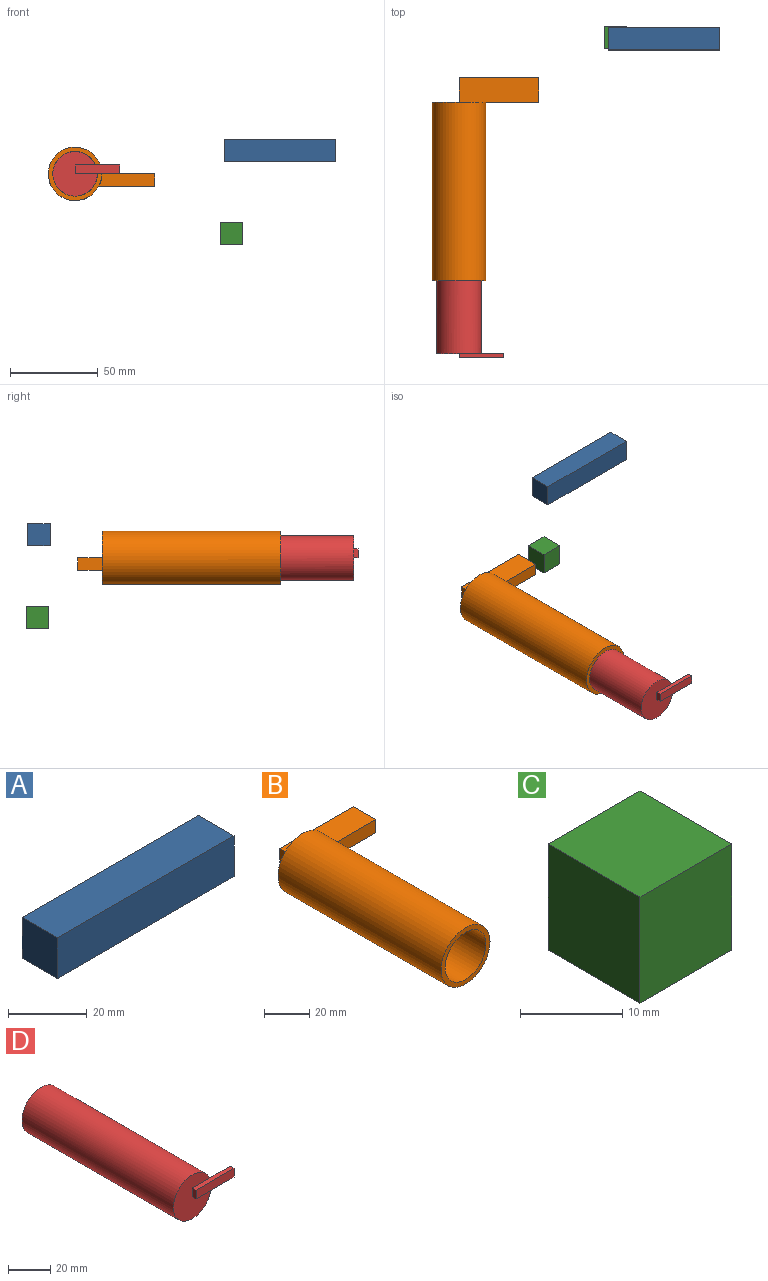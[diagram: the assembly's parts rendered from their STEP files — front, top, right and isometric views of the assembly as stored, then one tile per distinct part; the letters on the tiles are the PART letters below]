
ASSEMBLY  parts=4 mates=1
PART A: 6 faces, bbox 63.5x12.7x12.7 mm
  f0: plane 63.5x12.7mm, normal (0,0,-1), area 806.5mm2, adj f1,f3,f4,f5
  f1: plane 12.7x12.7mm, normal (1,0,0), area 161.3mm2, adj f0,f2,f4,f5
  f2: plane 63.5x12.7mm, normal (0,0,1), area 806.5mm2, adj f1,f3,f4,f5
  f3: plane 12.7x12.7mm, normal (-1,0,0), area 161.3mm2, adj f0,f2,f4,f5
  f4: plane 63.5x12.7mm, normal (0,-1,0), area 806.5mm2, adj f0,f1,f2,f3
  f5: plane 63.5x12.7mm, normal (0,1,0), area 806.5mm2, adj f0,f1,f2,f3
PART B: 11 faces, bbox 60.8x115.6x30.5 mm
  f0: cylinder r=15.24mm len=101.6mm, axis (0,1,0), area 9728.8mm2, adj f1,f2,f9
  f1: plane 30.48x30.48mm, normal (0,-1,0), area 223mm2, adj f0,f3
  f2: plane 30.48x30.48mm, normal (0,1,0), area 624.7mm2, adj f0,f5,f6,f7
  f3: cylinder r=12.7mm len=99.06mm, axis (0,1,0), area 7904.6mm2, adj f1,f4
  f4: plane 25.4x25.4mm, normal (0,-1,0), area 506.7mm2, adj f3
  f5: plane 45.53x14mm, normal (0,0,-1), area 637.3mm2, adj f2,f6,f8,f9,f10
  f6: plane 14x7.16mm, normal (-1,0,0), area 100.2mm2, adj f2,f5,f7,f10
  f7: plane 45.53x14mm, normal (0,0,1), area 637.3mm2, adj f2,f6,f8,f9,f10
  f8: plane 14x7.16mm, normal (1,0,0), area 100.2mm2, adj f5,f7,f9,f10
  f9: plane 32.08x7.16mm, normal (0,-1,0), area 221.1mm2, adj f0,f5,f7,f8
  f10: plane 45.53x7.16mm, normal (0,1,0), area 326.1mm2, adj f5,f6,f7,f8
PART C: 6 faces, bbox 12.7x12.7x12.7 mm
  f0: plane 12.7x12.7mm, normal (0,0,-1), area 161.3mm2, adj f1,f3,f4,f5
  f1: plane 12.7x12.7mm, normal (1,0,0), area 161.3mm2, adj f0,f2,f4,f5
  f2: plane 12.7x12.7mm, normal (0,0,1), area 161.3mm2, adj f1,f3,f4,f5
  f3: plane 12.7x12.7mm, normal (-1,0,0), area 161.3mm2, adj f0,f2,f4,f5
  f4: plane 12.7x12.7mm, normal (0,-1,0), area 161.3mm2, adj f0,f1,f2,f3
  f5: plane 12.7x12.7mm, normal (0,1,0), area 161.3mm2, adj f0,f1,f2,f3
PART D: 9 faces, bbox 38.1x104.1x25.4 mm
  f0: plane 25.4x25.4mm, normal (0,-1,0), area 444mm2, adj f1,f4,f5,f6
  f1: cylinder r=12.7mm len=101.6mm, axis (0,1,0), area 8107.3mm2, adj f0,f2,f3
  f2: plane 25.4x25.4mm, normal (0,1,0), area 506.7mm2, adj f1
  f3: plane 13.76x5.08mm, normal (0,1,0), area 66.3mm2, adj f1,f4,f6,f7
  f4: plane 25.4x2.54mm, normal (0,0,1), area 64.5mm2, adj f0,f3,f5,f7,f8
  f5: plane 5.08x2.54mm, normal (-1,0,0), area 12.9mm2, adj f0,f4,f6,f8
  f6: plane 25.4x2.54mm, normal (0,0,-1), area 64.5mm2, adj f0,f3,f5,f7,f8
  f7: plane 5.08x2.54mm, normal (1,0,0), area 12.9mm2, adj f3,f4,f6,f8
  f8: plane 25.4x5.08mm, normal (0,-1,0), area 129mm2, adj f4,f5,f6,f7
PLACE A t=(41.47,6.48,65.27)mm
PLACE B t=(-78.61,-36,8.51)mm
PLACE C t=(10.74,7.51,-53.92)mm
PLACE D t=(-78.61,-77.6,8.51)mm
MATE slider D.f1 <-> B.f0  axis (0,1,0) through (-78.61,-77.6,8.51)mm
